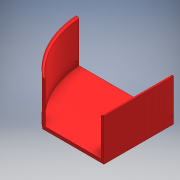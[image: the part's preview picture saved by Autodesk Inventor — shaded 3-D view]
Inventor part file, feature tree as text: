
AUTODESK INVENTOR PART (.ipt)
format: ipt  version: 2016 (Build 200138000, 138)  size: 171,520 bytes
history: native  units: in
note: dims shown in document units (in); Inventor stores cm internally (conversion verified against a paired STEP export)
features: sketch x5, extrude x2, split x1, hole x1, fillet x1, pattern_linear x1
ambient origin geometry x8: Origin, YZ Plane, XZ Plane, XY Plane, X Axis, Y Axis, Z Axis, Center Point
bodies: Solid1 (feature_tree)
feature tree (11):
  extrude  "Extrusion1"  Depth=0.125in
  split  "Split2"
  sketch  "Sketch10"  dims[d119=1.0in d120=1.0in d107=0.1575in d108=0.75in d109=0.375in d110=0.25in d111=0.5635in d112=1.0in d113=0.8108in d114=3.5433in d116=0.6299in d134=4.0in d135=0.2in d136=0.125in d34=1.0in d35=1.0in d80=1.0in d81=1.0in]
  extrude  "Extrusion3"  Depth=5.0in TaperAngle=0.0deg
  hole  "Hole2"  [1 undecoded]
  fillet  "Fillet2"  Radius=0.2in
  sketch  "Sketch7"  dims[d103=3.0in d104=0.0in]
  pattern_linear  "Rectangular Pattern2"  Count1=9 Spacing1=0.6299in
  sketch  "Sketch1"  dims[d0=7.0in d4=0.125in]
  sketch  "Sketch5"  dims[d6=0.075in d32=5.0in d33=0.0in]
  sketch  "Sketch6"  dims[d87=3.0in d99=0.2in d100=0.2in]
note: 1 required parameter value undecoded (feature->parameter linkage not recoverable at this tier; creation-order binding heuristic only, values carry confidence <= 0.55)
